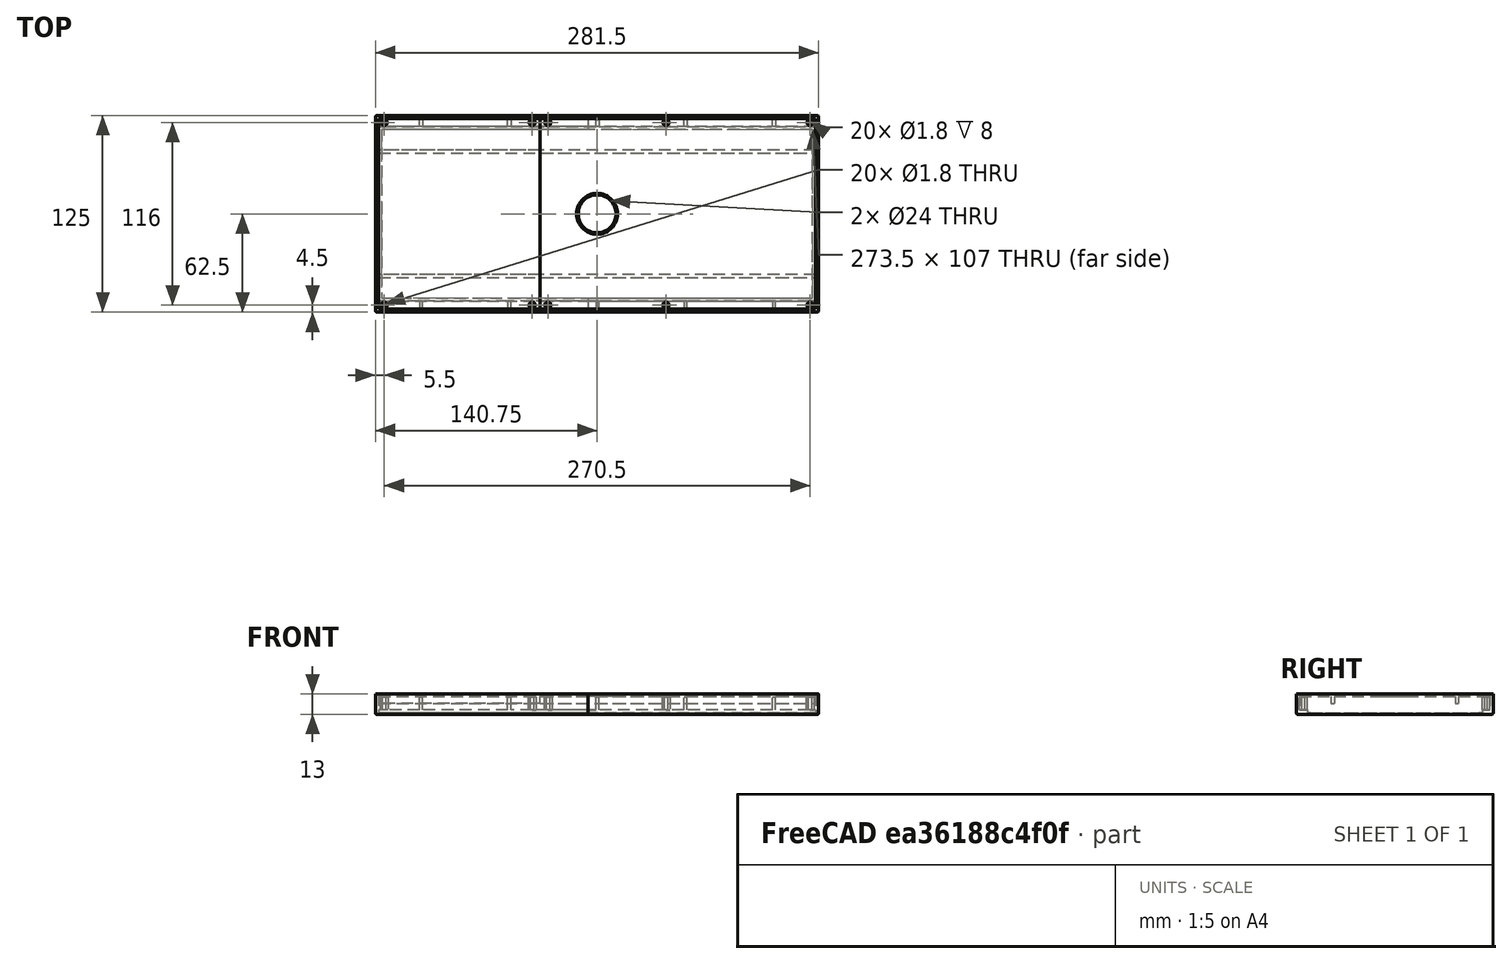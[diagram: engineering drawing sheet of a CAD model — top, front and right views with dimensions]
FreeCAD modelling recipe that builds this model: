
FCSTD DOCUMENT  (FreeCAD 0.20R29177 +426 (Git))
Label: Multisolarpanel-Screws
License: All rights reserved
LicenseURL: http://en.wikipedia.org/wiki/All_rights_reserved
objects: Sketcher::SketchObject×10, PartDesign::Pocket×6, Part::FeaturePython×6, PartDesign::Pad×4, Spreadsheet::Sheet×2, PartDesign::Plane×2, PartDesign::Body×2, App::DocumentObjectGroup×2, PartDesign::Chamfer×1, PartDesign::Fillet×1
note: 44 computed .brp shape members not serialized (recipe doc carries the construction recipe); baked Part::Feature solids carry a one-line shape summary decoded from their .brp

FEATURE [Spreadsheet::Sheet] Spreadsheet  label="Globals"
  cells = A2=Number of Panels; B2(NumberOfPanels)=5; A3=Panel Length; B3(PanelLength)==111mm; A4=Panel Width; B4(PanelWidth)==55mm; A5=Panel Height; B5(PanelHeight)==3.5mm; A7=Frame Width; B7(FrameWidth)==2mm; A8=Frame Height; B8(FrameHeight)==PlexiglasHeight + ScrewFixHeight + FrameWidth + 1mm; D8=Calculated; A9=Plexiglas Height; B9(PlexiglasHeight)==2mm; A10=Plexiglas Length; B10(PlexiglasLength)==(PanelWidth + FitPrecision) * NumberOfPanels; D10=Calculated; A11=Plexiglas Width; B11(PlexiglasWidth)==PanelLength; D11=Calculated; A12=Bottom Height (calculated); B12(BottomHeight)==FrameHeight - PlexiglasHeight - PanelHeight; D12=Calculated; A14=ScrewR; B14(ScrewR)==1mm; A15=ScrewFixHeight; B15(ScrewFixHeight)==8mm; A16=ScrewFixR; B16(ScrewFixR)==2.5mm; A18=BackPanel Width; B18(BackPanelWidth)==(PanelWidth + FitPrecision) * NumberOfPanels / 3; A22=Corner Length; B22(CornerLength)==5mm; A23=Corner Width; B23(CornerWidth)==1.5mm; A24=Corner Height; B24(CornerHeight)==PanelHeight; D24=Calculated; A25=Fit Precision; B25(FitPrecision)==0.5mm; A27=Connector Diameter; B27(ConnectorDiameter)==4.9mm; A29=FixThickness; B29(FixThickness)==2mm; A30=FixOuter (calculated); B30==PanelWidth + 2 * FrameWidth; D30=Calculated; A31=FixHeight; B31(FixHeight)==6mm; A32=HandsLength; B32(HandsLength)==4mm; A33=HandsDiameter; B33(HandsDiameter)==2mm; A35=BayonetInner; B35(BayonetInner)==B30 - 2 * FixThickness; D35=Calculated; A36=BayonetHeight; B36(BayonetHeight)==10mm
FEATURE [Spreadsheet::Sheet] Spreadsheet001  label="BayonetVars"
  cells = A2=InnerOuterRingR; B2(InnerOuterRingR)==20mm; A3=InnerRingWidth; B3(InnerRingWidth)==8mm; A4=InnerRingHeight; B4(InnerRingHeight)==15mm; A5=InnerBaseHeight; B5(InnerBaseHeight)==2mm; A6=OuterRingWidth; B6(OuterRingWidth)==5mm; A7=OuterRingHeight; B7(OuterRingHeight)==InnerRingHeight; A8=PinR; B8(PinR)==5mm; A9=PinDownPath; B9(PinDownPath)==InnerRingHeight / 2; A10=NumberOfPins; B10(NumberOfPins)=3; A11=FitPrecision; B11(FitPrecision)==0.5mm
FEATURE [Sketcher::SketchObject] Sketch012  label="WindowBase"
  FullyConstrained = true
  MapMode = 5
  Support = -> [XY_Plane003]
  expr: Constraints[10] = <<Globals>>.PlexiglasLength + <<Globals>>.FrameWidth * 2
  expr: Constraints[11] = <<Globals>>.PlexiglasWidth + <<Globals>>.ScrewFixR * 4 + <<Globals>>.FrameWidth * 2
  sketch-geometry (5):
    g0: LineSegment StartX=140.75 StartY=-62.5 StartZ=0 EndX=140.75 EndY=62.5 EndZ=0
    g1: LineSegment StartX=140.75 StartY=62.5 StartZ=0 EndX=-140.75 EndY=62.5 EndZ=0
    g2: LineSegment StartX=-140.75 StartY=62.5 StartZ=0 EndX=-140.75 EndY=-62.5 EndZ=0
    g3: LineSegment StartX=-140.75 StartY=-62.5 StartZ=0 EndX=140.75 EndY=-62.5 EndZ=0
    g4: GeomPoint X=0 Y=0 Z=0
  constraints (12):
    c: Coincident(g0,g1)
    c: Coincident(g1,g2)
    c: Coincident(g2,g3)
    c: Coincident(g3,g0)
    c: Horizontal(g1)
    c: Horizontal(g3)
    c: Vertical(g0)
    c: Vertical(g2)
    c: Symmetric(g1,g0,g4)
    c: Coincident(g4,g-1)
    c: DistanceX(g1,g1) = 281.5
    c: DistanceY(g2,g2) = 125
FEATURE [PartDesign::Pad] Pad006  label="TopBase"
  Direction = (0,0,1)
  Length = 13
  Length2 = 10
  Profile = -> Sketch012
  ReferenceAxis = -> Sketch012 [N_Axis]
  Refine = true
  Type = 0
  expr: Length = <<Globals>>.FrameHeight
FEATURE [Sketcher::SketchObject] Sketch013  label="PlexiglasSketch"
  FullyConstrained = true
  MapMode = 5
  Placement = pos=(0,0,13) rot=(0,0,1;0rad)
  Support = -> [Pad006]
  expr: Constraints[10] = <<Globals>>.PlexiglasLength
  expr: Constraints[11] = <<Globals>>.PlexiglasWidth
  sketch-geometry (5):
    g0: LineSegment StartX=138.75 StartY=-55.5 StartZ=0 EndX=138.75 EndY=55.5 EndZ=0
    g1: LineSegment StartX=138.75 StartY=55.5 StartZ=0 EndX=-138.75 EndY=55.5 EndZ=0
    g2: LineSegment StartX=-138.75 StartY=55.5 StartZ=0 EndX=-138.75 EndY=-55.5 EndZ=0
    g3: LineSegment StartX=-138.75 StartY=-55.5 StartZ=0 EndX=138.75 EndY=-55.5 EndZ=0
    g4: GeomPoint X=0 Y=0 Z=0
  constraints (12):
    c: Coincident(g0,g1)
    c: Coincident(g1,g2)
    c: Coincident(g2,g3)
    c: Coincident(g3,g0)
    c: Horizontal(g1)
    c: Horizontal(g3)
    c: Vertical(g0)
    c: Vertical(g2)
    c: Symmetric(g1,g0,g4)
    c: Coincident(g4,g-1)
    c: DistanceX(g1,g1) = 277.5
    c: DistanceY(g2,g2) = 111
FEATURE [PartDesign::Pocket] Pocket003  label="PlexiglasBase"
  BaseFeature = -> Pad006
  Direction = (0,0,-1)
  Length = 12
  Length2 = 5
  Profile = -> Sketch013
  ReferenceAxis = -> Sketch013 [N_Axis]
  Refine = true
  Type = 0
  expr: Length = <<Globals>>.FrameHeight - 1mm
FEATURE [Sketcher::SketchObject] Sketch014  label="WindowSketch"
  FullyConstrained = true
  MapMode = 5
  Placement = pos=(0,0,1) rot=(0,0,1;0rad)
  Support = -> [Pocket003]
  expr: Constraints[10] = <<Globals>>.PlexiglasLength - <<Globals>>.FrameWidth * 2
  expr: Constraints[11] = <<Globals>>.PlexiglasWidth - <<Globals>>.FrameWidth * 2
  sketch-geometry (5):
    g0: LineSegment StartX=136.75 StartY=-53.5 StartZ=0 EndX=136.75 EndY=53.5 EndZ=0
    g1: LineSegment StartX=136.75 StartY=53.5 StartZ=0 EndX=-136.75 EndY=53.5 EndZ=0
    g2: LineSegment StartX=-136.75 StartY=53.5 StartZ=0 EndX=-136.75 EndY=-53.5 EndZ=0
    g3: LineSegment StartX=-136.75 StartY=-53.5 StartZ=0 EndX=136.75 EndY=-53.5 EndZ=0
    g4: GeomPoint X=0 Y=0 Z=0
  constraints (12):
    c: Coincident(g0,g1)
    c: Coincident(g1,g2)
    c: Coincident(g2,g3)
    c: Coincident(g3,g0)
    c: Horizontal(g1)
    c: Horizontal(g3)
    c: Vertical(g0)
    c: Vertical(g2)
    c: Symmetric(g1,g0,g4)
    c: Coincident(g4,g-1)
    c: DistanceX(g1,g1) = 273.5
    c: DistanceY(g2,g2) = 107
FEATURE [PartDesign::Pocket] Pocket004  label="Window"
  BaseFeature = -> Pocket003
  Direction = (0,0,-1)
  Length = 5
  Length2 = 5
  Profile = -> Sketch014
  ReferenceAxis = -> Sketch014 [N_Axis]
  Refine = true
  Type = 1
FEATURE [Sketcher::SketchObject] Sketch015  label="FrameSketch"
  FullyConstrained = true
  MapMode = 5
  Placement = pos=(0,0,13) rot=(0,0,1;0rad)
  Support = -> [Pocket004]
  expr: .Constraints.FrameLength = <<Globals>>.PlexiglasLength
  expr: .Constraints.FrameWidth = <<Globals>>.PlexiglasWidth + <<Globals>>.ScrewFixR * 4
  sketch-geometry (5):
    g0: LineSegment StartX=138.75 StartY=-60.5 StartZ=0 EndX=138.75 EndY=60.5 EndZ=0
    g1: LineSegment StartX=138.75 StartY=60.5 StartZ=0 EndX=-138.75 EndY=60.5 EndZ=0
    g2: LineSegment StartX=-138.75 StartY=60.5 StartZ=0 EndX=-138.75 EndY=-60.5 EndZ=0
    g3: LineSegment StartX=-138.75 StartY=-60.5 StartZ=0 EndX=138.75 EndY=-60.5 EndZ=0
    g4: GeomPoint X=0 Y=0 Z=0
  constraints (12):
    c: Coincident(g0,g1)
    c: Coincident(g1,g2)
    c: Coincident(g2,g3)
    c: Coincident(g3,g0)
    c: Horizontal(g1)
    c: Horizontal(g3)
    c: Vertical(g0)
    c: Vertical(g2)
    c: Symmetric(g1,g0,g4)
    c: Coincident(g4,g-1)
    c: DistanceX(g1,g1) = 277.5  'FrameLength'
    c: DistanceY(g2,g2) = 121  'FrameWidth'
FEATURE [PartDesign::Pocket] Pocket005  label="Frame"
  BaseFeature = -> Pocket004
  Direction = (0,0,-1)
  Length = 10
  Length2 = 5
  Profile = -> Sketch015
  ReferenceAxis = -> Sketch015 [N_Axis]
  Refine = true
  Type = 0
  expr: Length = <<Globals>>.FrameHeight - <<Globals>>.PlexiglasHeight - 1mm
FEATURE [Sketcher::SketchObject] Sketch016  label="ScrewFixesAndPanelGuidesSketch"
  ExternalGeometry = -> [Sketch015]
  FullyConstrained = false
  MapMode = 5
  Placement = pos=(0,0,3) rot=(0,0,1;0rad)
  Support = -> [Pocket005]
  expr: Constraints[0] = <<Globals>>.ScrewFixR
  expr: Constraints[29] = <<Globals>>.ScrewFixR + 1mm
  expr: Constraints[39] = <<Globals>>.ScrewFixR * 2
  expr: Constraints[40] = <<Globals>>.FrameWidth
  sketch-geometry (51):
    g0: Circle CenterX=-135.25 CenterY=58 CenterZ=0 NormalX=0 NormalY=0 NormalZ=1 AngleXU=0 Radius=2.5
    g1: Circle CenterX=-135.25 CenterY=-58 CenterZ=0 NormalX=0 NormalY=0 NormalZ=1 AngleXU=0 Radius=2.5
    g2: Circle CenterX=-41.25 CenterY=58 CenterZ=0 NormalX=0 NormalY=0 NormalZ=1 AngleXU=0 Radius=2.5
    g3: Circle CenterX=43.75 CenterY=58 CenterZ=0 NormalX=0 NormalY=0 NormalZ=1 AngleXU=0 Radius=2.5
    g4: Circle CenterX=-41.25 CenterY=-58 CenterZ=0 NormalX=0 NormalY=0 NormalZ=1 AngleXU=0 Radius=2.5
    g5: Circle CenterX=43.75 CenterY=-58 CenterZ=0 NormalX=0 NormalY=0 NormalZ=1 AngleXU=0 Radius=2.5
    g6: Circle CenterX=135.25 CenterY=58 CenterZ=0 NormalX=0 NormalY=0 NormalZ=1 AngleXU=0 Radius=2.5
    g7: Circle CenterX=135.25 CenterY=-58 CenterZ=0 NormalX=0 NormalY=0 NormalZ=1 AngleXU=0 Radius=2.5
    g8: GeomPoint X=-137.75 Y=58 Z=0
    g9: Circle CenterX=-31.25 CenterY=58 CenterZ=0 NormalX=0 NormalY=0 NormalZ=1 AngleXU=0 Radius=2.5
    g10: Circle CenterX=-31.25 CenterY=-58 CenterZ=0 NormalX=0 NormalY=0 NormalZ=1 AngleXU=0 Radius=2.5
    g11: LineSegment StartX=-112.75 StartY=60.5 StartZ=0 EndX=-110.75 EndY=60.5 EndZ=0
    g12: LineSegment StartX=-110.75 StartY=60.5 StartZ=0 EndX=-110.75 EndY=55.5 EndZ=0
    g13: LineSegment StartX=-110.75 StartY=55.5 StartZ=0 EndX=-112.75 EndY=55.5 EndZ=0
    g14: LineSegment StartX=-112.75 StartY=55.5 StartZ=0 EndX=-112.75 EndY=60.5 EndZ=0
    g15: LineSegment StartX=-56.75 StartY=60.5 StartZ=0 EndX=-54.75 EndY=60.5 EndZ=0
    g16: LineSegment StartX=-54.75 StartY=60.5 StartZ=0 EndX=-54.75 EndY=55.5 EndZ=0
    g17: LineSegment StartX=-54.75 StartY=55.5 StartZ=0 EndX=-56.75 EndY=55.5 EndZ=0
    g18: LineSegment StartX=-56.75 StartY=55.5 StartZ=0 EndX=-56.75 EndY=60.5 EndZ=0
    g19: LineSegment StartX=-0.75 StartY=60.5 StartZ=0 EndX=1.25 EndY=60.5 EndZ=0
    g20: LineSegment StartX=1.25 StartY=60.5 StartZ=0 EndX=1.25 EndY=55.5 EndZ=0
    g21: LineSegment StartX=1.25 StartY=55.5 StartZ=0 EndX=-0.75 EndY=55.5 EndZ=0
    g22: LineSegment StartX=-0.75 StartY=55.5 StartZ=0 EndX=-0.75 EndY=60.5 EndZ=0
    g23: LineSegment StartX=55.25 StartY=60.5 StartZ=0 EndX=57.25 EndY=60.5 EndZ=0
    g24: LineSegment StartX=57.25 StartY=60.5 StartZ=0 EndX=57.25 EndY=55.5 EndZ=0
    g25: LineSegment StartX=57.25 StartY=55.5 StartZ=0 EndX=55.25 EndY=55.5 EndZ=0
    g26: LineSegment StartX=55.25 StartY=55.5 StartZ=0 EndX=55.25 EndY=60.5 EndZ=0
    g27: LineSegment StartX=111.25 StartY=60.5 StartZ=0 EndX=113.25 EndY=60.5 EndZ=0
    g28: LineSegment StartX=113.25 StartY=60.5 StartZ=0 EndX=113.25 EndY=55.5 EndZ=0
    g29: LineSegment StartX=113.25 StartY=55.5 StartZ=0 EndX=111.25 EndY=55.5 EndZ=0
    g30: LineSegment StartX=111.25 StartY=55.5 StartZ=0 EndX=111.25 EndY=60.5 EndZ=0
    g31: LineSegment StartX=-112.75 StartY=-60.5 StartZ=0 EndX=-110.75 EndY=-60.5 EndZ=0
    g32: LineSegment StartX=-110.75 StartY=-60.5 StartZ=0 EndX=-110.75 EndY=-55.5 EndZ=0
    g33: LineSegment StartX=-110.75 StartY=-55.5 StartZ=0 EndX=-112.75 EndY=-55.5 EndZ=0
    g34: LineSegment StartX=-112.75 StartY=-55.5 StartZ=0 EndX=-112.75 EndY=-60.5 EndZ=0
    g35: LineSegment StartX=-56.75 StartY=-60.5 StartZ=0 EndX=-54.75 EndY=-60.5 EndZ=0
    g36: LineSegment StartX=-54.75 StartY=-60.5 StartZ=0 EndX=-54.75 EndY=-55.5 EndZ=0
    g37: LineSegment StartX=-54.75 StartY=-55.5 StartZ=0 EndX=-56.75 EndY=-55.5 EndZ=0
    g38: LineSegment StartX=-56.75 StartY=-55.5 StartZ=0 EndX=-56.75 EndY=-60.5 EndZ=0
    g39: LineSegment StartX=-0.75 StartY=-60.5 StartZ=0 EndX=1.25 EndY=-60.5 EndZ=0
    g40: LineSegment StartX=1.25 StartY=-60.5 StartZ=0 EndX=1.25 EndY=-55.5 EndZ=0
    g41: LineSegment StartX=1.25 StartY=-55.5 StartZ=0 EndX=-0.75 EndY=-55.5 EndZ=0
    g42: LineSegment StartX=-0.75 StartY=-55.5 StartZ=0 EndX=-0.75 EndY=-60.5 EndZ=0
    g43: LineSegment StartX=55.25 StartY=-60.5 StartZ=0 EndX=57.25 EndY=-60.5 EndZ=0
    g44: LineSegment StartX=57.25 StartY=-60.5 StartZ=0 EndX=57.25 EndY=-55.5 EndZ=0
    g45: LineSegment StartX=57.25 StartY=-55.5 StartZ=0 EndX=55.25 EndY=-55.5 EndZ=0
    g46: LineSegment StartX=55.25 StartY=-55.5 StartZ=0 EndX=55.25 EndY=-60.5 EndZ=0
    g47: LineSegment StartX=111.25 StartY=-60.5 StartZ=0 EndX=113.25 EndY=-60.5 EndZ=0
    g48: LineSegment StartX=113.25 StartY=-60.5 StartZ=0 EndX=113.25 EndY=-55.5 EndZ=0
    g49: LineSegment StartX=113.25 StartY=-55.5 StartZ=0 EndX=111.25 EndY=-55.5 EndZ=0
    g50: LineSegment StartX=111.25 StartY=-55.5 StartZ=0 EndX=111.25 EndY=-60.5 EndZ=0
  constraints (132):
    c: Radius(g0) = 2.5
    c: Radius(g1) = 2.5
    c: Equal(g0,g2) = 2.5
    c: PointOnObject(g8,g0)
    c: DistanceX(g-3,g8) = 1  'X_Off_1'
    c: Vertical(g2,g4)
    c: Vertical(g0,g1)
    c: Vertical(g3,g5)
    c: Vertical(g6,g7)
    c: Horizontal(g6,g3)
    c: Horizontal(g3,g2)
    c: Horizontal(g2,g0)
    c: Equal(g2,g3)
    c: Equal(g3,g6)
    c: Equal(g6,g7)
    c: Equal(g7,g5)
    c: Equal(g5,g4)
    c: DistanceX(g0,g2) = 94  'X_Off_2'
    c: Horizontal(g1,g4)
    c: Horizontal(g4,g5)
    c: Horizontal(g5,g7)
    c: Tangent(g-4,g1)
    c: Equal(g2,g9)
    c: Horizontal(g9,g2)
    c: DistanceX(g2,g9) = 10  'X_Off_3'
    c: Equal(g10,g4)
    c: Horizontal(g10,g4)
    c: Vertical(g10,g9)
    c: Tangent(g0,g-6)
    c: DistanceX(g6,g-6) = 3.5
    c: Coincident(g11,g12)
    c: Coincident(g12,g13)
    c: Coincident(g13,g14)
    c: Coincident(g14,g11)
    c: Horizontal(g11)
    c: Horizontal(g13)
    c: Vertical(g12)
    c: Vertical(g14)
    c: PointOnObject(g11,g-6)
    c: DistanceY(g14,g14) = 5
    c: DistanceX(g13,g13) = 2
    c: DistanceX(g-6,g11) = 26
    c: Coincident(g15,g16)
    c: Coincident(g16,g17)
    c: Coincident(g17,g18)
    c: Coincident(g18,g15)
    c: Horizontal(g17)
    c: Vertical(g16)
    c: Vertical(g18)
    c: Equal(g14,g18) = 5
    c: Equal(g13,g17) = 2
    c: Coincident(g19,g20)
    c: Coincident(g20,g21)
    c: Coincident(g21,g22)
    c: Coincident(g22,g19)
    c: Horizontal(g21)
    c: Vertical(g20)
    c: Vertical(g22)
    c: Equal(g14,g22) = 5
    c: Equal(g13,g21) = 2
    c: Coincident(g23,g24)
    c: Coincident(g24,g25)
    c: Coincident(g25,g26)
    c: Coincident(g26,g23)
    c: Horizontal(g25)
    c: Vertical(g24)
    c: Vertical(g26)
    c: Equal(g14,g26) = 5
    c: Equal(g13,g25) = 2
    c: Coincident(g27,g28)
    c: Coincident(g28,g29)
    c: Coincident(g29,g30)
    c: Coincident(g30,g27)
    c: Horizontal(g29)
    c: Vertical(g28)
    c: Vertical(g30)
    c: Equal(g14,g30) = 5
    c: Equal(g13,g29) = 2
    c: Tangent(g27,g-6)
    c: Tangent(g23,g-6)
    c: Tangent(g19,g-6)
    c: Tangent(g-6,g15)
    c: DistanceX(g11,g15) = 56
    c: DistanceX(g15,g19) = 56
    c: DistanceX(g19,g23) = 56
    c: DistanceX(g23,g27) = 56
    c: Coincident(g31,g32)
    c: Coincident(g32,g33)
    c: Coincident(g33,g34)
    c: Coincident(g34,g31)
    c: Horizontal(g31)
    c: Horizontal(g33)
    c: Vertical(g32)
    c: Vertical(g34)
    c: Coincident(g35,g36)
    c: Coincident(g36,g37)
    c: Coincident(g37,g38)
    c: Coincident(g38,g35)
    c: Horizontal(g37)
    c: Vertical(g36)
    c: Vertical(g38)
    c: Equal(g34,g38) = 5
    c: Equal(g33,g37) = 2
    c: Coincident(g39,g40)
    c: Coincident(g40,g41)
    c: Coincident(g41,g42)
    c: Coincident(g42,g39)
    c: Horizontal(g41)
    c: Vertical(g40)
    c: Vertical(g42)
    c: Equal(g34,g42) = 5
    c: Equal(g33,g41) = 2
    c: Coincident(g43,g44)
    c: Coincident(g44,g45)
    c: Coincident(g45,g46)
    c: Coincident(g46,g43)
    c: Horizontal(g45)
    c: Vertical(g44)
    c: Vertical(g46)
    c: Equal(g34,g46) = 5
    c: Equal(g33,g45) = 2
    c: Coincident(g47,g48)
    c: Coincident(g48,g49)
    c: Coincident(g49,g50)
    c: Coincident(g50,g47)
    c: Horizontal(g49)
    c: Vertical(g48)
    c: Vertical(g50)
    c: Equal(g34,g50) = 5
    c: Equal(g33,g49) = 2
    c: Horizontal(g0,g8)
    c: DistanceX(g9,g3) = 75  'X_Off_4'
FEATURE [PartDesign::Pad] Pad  label="ScrewFixesAndPanelGuides"
  BaseFeature = -> Pocket005
  Direction = (0,0,1)
  Length = 8
  Length2 = 10
  Profile = -> Sketch016
  ReferenceAxis = -> Sketch016 [N_Axis]
  Refine = true
  Type = 0
  expr: Length = <<Globals>>.ScrewFixHeight
FEATURE [Sketcher::SketchObject] Sketch  label="ScrewHolesSketch"
  ExternalGeometry = -> [Sketch016]
  FullyConstrained = true
  MapMode = 5
  Placement = pos=(0,0,11) rot=(0,0,1;0rad)
  Support = -> [Pad]
  expr: Constraints[19] = <<Globals>>.ScrewR - 0.1mm
  sketch-geometry (10):
    g0: Circle CenterX=-135.25 CenterY=58 CenterZ=0 NormalX=0 NormalY=0 NormalZ=1 AngleXU=0 Radius=0.9
    g1: Circle CenterX=-41.25 CenterY=58 CenterZ=0 NormalX=0 NormalY=0 NormalZ=1 AngleXU=0 Radius=0.9
    g2: Circle CenterX=-31.25 CenterY=58 CenterZ=0 NormalX=0 NormalY=0 NormalZ=1 AngleXU=0 Radius=0.9
    g3: Circle CenterX=43.75 CenterY=58 CenterZ=0 NormalX=0 NormalY=0 NormalZ=1 AngleXU=0 Radius=0.9
    g4: Circle CenterX=135.25 CenterY=58 CenterZ=0 NormalX=0 NormalY=0 NormalZ=1 AngleXU=0 Radius=0.9
    g5: Circle CenterX=135.25 CenterY=-58 CenterZ=0 NormalX=0 NormalY=0 NormalZ=1 AngleXU=0 Radius=0.9
    g6: Circle CenterX=43.75 CenterY=-58 CenterZ=0 NormalX=0 NormalY=0 NormalZ=1 AngleXU=0 Radius=0.9
    g7: Circle CenterX=-31.25 CenterY=-58 CenterZ=0 NormalX=0 NormalY=0 NormalZ=1 AngleXU=0 Radius=0.9
    g8: Circle CenterX=-41.25 CenterY=-58 CenterZ=0 NormalX=0 NormalY=0 NormalZ=1 AngleXU=0 Radius=0.9
    g9: Circle CenterX=-135.25 CenterY=-58 CenterZ=0 NormalX=0 NormalY=0 NormalZ=1 AngleXU=0 Radius=0.9
  constraints (20):
    c: Coincident(g0,g-3)
    c: Coincident(g1,g-4)
    c: Coincident(g2,g-11)
    c: Coincident(g3,g-5)
    c: Coincident(g4,g-6)
    c: Coincident(g5,g-7)
    c: Coincident(g6,g-8)
    c: Coincident(g7,g-12)
    c: Coincident(g8,g-9)
    c: Coincident(g9,g-10)
    c: Equal(g0,g1)
    c: Equal(g1,g2)
    c: Equal(g2,g3)
    c: Equal(g3,g4)
    c: Equal(g4,g5)
    c: Equal(g5,g6)
    c: Equal(g6,g7)
    c: Equal(g7,g8)
    c: Equal(g8,g9)
    c: Radius(g0) = 0.9
FEATURE [PartDesign::Pocket] Pocket  label="ScrewHoles"
  BaseFeature = -> Pad
  Direction = (0,0,-1)
  Length = 8
  Length2 = 5
  Profile = -> Sketch
  ReferenceAxis = -> Sketch [N_Axis]
  Refine = true
  Type = 0
  expr: Length = <<Globals>>.ScrewFixHeight
FEATURE [Sketcher::SketchObject] Sketch017  label="BackPlaneSketch"
  FullyConstrained = true
  MapMode = 5
  Placement = pos=(0,0,13) rot=(0,0,1;0rad)
  expr: Constraints[10] = <<FrameSketch>>.Constraints.FrameLength
  expr: Constraints[11] = <<FrameSketch>>.Constraints.FrameWidth
  sketch-geometry (5):
    g0: LineSegment StartX=138.75 StartY=-60.5 StartZ=0 EndX=138.75 EndY=60.5 EndZ=0
    g1: LineSegment StartX=138.75 StartY=60.5 StartZ=0 EndX=-138.75 EndY=60.5 EndZ=0
    g2: LineSegment StartX=-138.75 StartY=60.5 StartZ=0 EndX=-138.75 EndY=-60.5 EndZ=0
    g3: LineSegment StartX=-138.75 StartY=-60.5 StartZ=0 EndX=138.75 EndY=-60.5 EndZ=0
    g4: GeomPoint X=0 Y=0 Z=0
  constraints (12):
    c: Coincident(g0,g1)
    c: Coincident(g1,g2)
    c: Coincident(g2,g3)
    c: Coincident(g3,g0)
    c: Horizontal(g1)
    c: Horizontal(g3)
    c: Vertical(g0)
    c: Vertical(g2)
    c: Symmetric(g1,g0,g4)
    c: Coincident(g4,g-1)
    c: DistanceX(g1,g1) = 277.5
    c: DistanceY(g2,g2) = 121
FEATURE [PartDesign::Pad] Pad007  label="BackPlane"
  Direction = (0,0,1)
  Length = 1.5
  Length2 = 10
  Placement = pos=(0,0,13) rot=(0,0,1;0rad)
  Profile = -> Sketch017
  ReferenceAxis = -> Sketch017 [N_Axis]
  Refine = true
  Reversed = true
  Type = 0
FEATURE [Sketcher::SketchObject] Sketch018  label="ScrewHolesSketch001"
  ExternalGeometry = -> [Sketch017]
  FullyConstrained = true
  MapMode = 5
  Placement = pos=(0,0,11.5) rot=(1,0,0;3.14159rad)
  Support = -> [Pad007]
  expr: Constraints[10] = <<ScrewFixesAndPanelGuidesSketch>>.Constraints.X_Off_1 + <<Globals>>.ScrewFixR
  expr: Constraints[11] = <<ScrewFixesAndPanelGuidesSketch>>.Constraints.X_Off_2
  expr: Constraints[12] = <<ScrewFixesAndPanelGuidesSketch>>.Constraints.X_Off_3
  expr: Constraints[13] = <<ScrewFixesAndPanelGuidesSketch>>.Constraints.X_Off_4
  expr: Constraints[14] = <<ScrewFixesAndPanelGuidesSketch>>.Constraints.X_Off_1 + <<Globals>>.ScrewFixR
  expr: Constraints[19] = <<Globals>>.ScrewFixR
  expr: Constraints[28] = <<Globals>>.ScrewFixR
  expr: Constraints[9] = <<Globals>>.ScrewR - 0.1mm
  sketch-geometry (10):
    g0: Circle CenterX=-135.25 CenterY=58 CenterZ=0 NormalX=0 NormalY=0 NormalZ=1 AngleXU=0 Radius=0.9
    g1: Circle CenterX=-41.25 CenterY=58 CenterZ=0 NormalX=0 NormalY=0 NormalZ=1 AngleXU=0 Radius=0.9
    g2: Circle CenterX=-31.25 CenterY=58 CenterZ=0 NormalX=0 NormalY=0 NormalZ=1 AngleXU=0 Radius=0.9
    g3: Circle CenterX=43.75 CenterY=58 CenterZ=0 NormalX=0 NormalY=0 NormalZ=1 AngleXU=0 Radius=0.9
    g4: Circle CenterX=135.25 CenterY=58 CenterZ=0 NormalX=0 NormalY=0 NormalZ=1 AngleXU=0 Radius=0.9
    g5: Circle CenterX=135.25 CenterY=-58 CenterZ=0 NormalX=0 NormalY=0 NormalZ=1 AngleXU=0 Radius=0.9
    g6: Circle CenterX=43.75 CenterY=-58 CenterZ=0 NormalX=0 NormalY=0 NormalZ=1 AngleXU=0 Radius=0.9
    g7: Circle CenterX=-31.25 CenterY=-58 CenterZ=0 NormalX=0 NormalY=0 NormalZ=1 AngleXU=0 Radius=0.9
    g8: Circle CenterX=-41.25 CenterY=-58 CenterZ=0 NormalX=0 NormalY=0 NormalZ=1 AngleXU=0 Radius=0.9
    g9: Circle CenterX=-135.25 CenterY=-58 CenterZ=0 NormalX=0 NormalY=0 NormalZ=1 AngleXU=0 Radius=0.9
  constraints (30):
    c: Equal(g0,g1)
    c: Equal(g1,g2)
    c: Equal(g2,g3)
    c: Equal(g3,g4)
    c: Equal(g4,g5)
    c: Equal(g5,g6)
    c: Equal(g6,g7)
    c: Equal(g7,g8)
    c: Equal(g8,g9)
    c: Radius(g0) = 0.9
    c: DistanceX(g-4,g0) = 3.5
    c: DistanceX(g0,g1) = 94
    c: DistanceX(g1,g2) = 10
    c: DistanceX(g2,g3) = 75
    c: DistanceX(g4,g-5) = 3.5
    c: Horizontal(g4,g3)
    c: Horizontal(g3,g2)
    c: Horizontal(g2,g1)
    c: Horizontal(g1,g0)
    c: DistanceY(g0,g-4) = 2.5
    c: Vertical(g0,g9)
    c: Vertical(g1,g8)
    c: Vertical(g7,g2)
    c: Vertical(g3,g6)
    c: Vertical(g4,g5)
    c: Horizontal(g5,g6)
    c: Horizontal(g6,g8)
    c: Horizontal(g8,g9)
    c: DistanceY(g-6,g9) = 2.5
    c: Horizontal(g7,g8)
FEATURE [PartDesign::Pocket] Pocket006  label="PlaneWithScrewHoles"
  BaseFeature = -> Pad007
  Direction = (0,0,1)
  Length = 5
  Length2 = 5
  Placement = pos=(0,0,13) rot=(0,0,1;0rad)
  Profile = -> Sketch018
  ReferenceAxis = -> Sketch018 [N_Axis]
  Refine = true
  Type = 1
FEATURE [Sketcher::SketchObject] Sketch025
  ExternalGeometry = -> [Pocket006]
  FullyConstrained = true
  MapMode = 5
  Placement = pos=(0,0,11.5) rot=(1,0,0;3.14159rad)
  Support = -> [Pocket006]
  expr: Constraints[21] = <<Globals>>.FrameWidth
  expr: Constraints[22] = <<Globals>>.FrameWidth
  sketch-geometry (8):
    g0: LineSegment StartX=-138.75 StartY=40.5 StartZ=0 EndX=138.75 EndY=40.5 EndZ=0
    g1: LineSegment StartX=138.75 StartY=40.5 StartZ=0 EndX=138.75 EndY=38.5 EndZ=0
    g2: LineSegment StartX=138.75 StartY=38.5 StartZ=0 EndX=-138.75 EndY=38.5 EndZ=0
    g3: LineSegment StartX=-138.75 StartY=38.5 StartZ=0 EndX=-138.75 EndY=40.5 EndZ=0
    g4: LineSegment StartX=-138.75 StartY=-38.5 StartZ=0 EndX=138.75 EndY=-38.5 EndZ=0
    g5: LineSegment StartX=138.75 StartY=-38.5 StartZ=0 EndX=138.75 EndY=-40.5 EndZ=0
    g6: LineSegment StartX=138.75 StartY=-40.5 StartZ=0 EndX=-138.75 EndY=-40.5 EndZ=0
    g7: LineSegment StartX=-138.75 StartY=-40.5 StartZ=0 EndX=-138.75 EndY=-38.5 EndZ=0
  constraints (24):
    c: Coincident(g0,g1)
    c: Coincident(g1,g2)
    c: Coincident(g2,g3)
    c: Coincident(g3,g0)
    c: Horizontal(g0)
    c: Horizontal(g2)
    c: Vertical(g1)
    c: Vertical(g3)
    c: PointOnObject(g0,g-4)
    c: PointOnObject(g1,g-6)
    c: Coincident(g4,g5)
    c: Coincident(g5,g6)
    c: Coincident(g6,g7)
    c: Coincident(g7,g4)
    c: Horizontal(g4)
    c: Horizontal(g6)
    c: Vertical(g5)
    c: Vertical(g7)
    c: PointOnObject(g4,g-4)
    c: PointOnObject(g5,g-6)
    c: DistanceY(g-5,g6) = 20
    c: DistanceY(g6,g4) = 2
    c: DistanceY(g2,g0) = 2
    c: DistanceY(g0,g-4) = 20
FEATURE [PartDesign::Pad] Pad009  label="Rails"
  BaseFeature = -> Pocket006
  Direction = (0,0,-1)
  Length = 4.5
  Length2 = 10
  Placement = pos=(0,0,13) rot=(0,0,1;0rad)
  Profile = -> Sketch025
  ReferenceAxis = -> Sketch025 [N_Axis]
  Refine = true
  Type = 0
  expr: Length = <<Globals>>.ScrewFixHeight - <<Globals>>.PanelHeight
FEATURE [PartDesign::Plane] DatumPlane001  label="CutPlane2"
  AttachmentOffset = pos=(0,0,-102.5) rot=(0,0,1;0rad)
  Length = 136.556
  MapMode = 4
  Placement = pos=(-36.25,0,0) rot=(0.57735,-0.57735,-0.57735;2.0944rad)
  ResizeMode = 0
  Width = 65.5563
FEATURE [Sketcher::SketchObject] Sketch026  label="CableHoleSketch"
  FullyConstrained = true
  MapMode = 5
  Placement = pos=(0,0,13) rot=(0,0,1;0rad)
  Support = -> [Pad009]
  expr: Constraints[1] = <<BayonetVars>>.InnerOuterRingR - <<BayonetVars>>.InnerRingWidth
  sketch-geometry (1):
    g0: Circle CenterX=0 CenterY=0 CenterZ=0 NormalX=0 NormalY=0 NormalZ=1 AngleXU=0 Radius=12
  constraints (2):
    c: Coincident(g0,g-1)
    c: Radius(g0) = 12
FEATURE [PartDesign::Plane] DatumPlane  label="CutPlane1"
  AttachmentOffset = pos=(0,0,-135) rot=(0,0,1;0rad)
  Length = 140.811
  MapMode = 4
  Placement = pos=(-5.75,0,0) rot=(0.57735,-0.57735,-0.57735;2.0944rad)
  ResizeMode = 0
  Width = 65.8114
FEATURE [PartDesign::Pocket] Pocket007  label="CableHole"
  BaseFeature = -> Pad009
  Direction = (0,0,-1)
  Length = 5
  Length2 = 5
  Placement = pos=(0,0,13) rot=(0,0,1;0rad)
  Profile = -> Sketch026
  ReferenceAxis = -> Sketch026 [N_Axis]
  Refine = true
  Type = 1
FEATURE [PartDesign::Chamfer] Chamfer
  Angle = 45
  Base = -> Pocket007 [Edge32,Edge31,Edge30,Edge29,Edge28,Edge33,Edge34,Edge35,Edge37,Edge38,Edge36]
  BaseFeature = -> Pocket007
  ChamferType = 0
  FlipDirection = false
  Placement = pos=(0,0,13) rot=(0,0,1;0rad)
  Refine = true
  Size = 1
  Size2 = 1
  SupportTransform = false
  UseAllEdges = false
FEATURE [PartDesign::Body] Body  label="BackPanel"
  Group = -> [Sketch017,Pad007,Sketch018,Pocket006,Sketch025,Pad009,DatumPlane001,Sketch026,Pocket007,Chamfer]
  Origin = -> Origin
  Tip = -> Chamfer
FEATURE [PartDesign::Fillet] Fillet
  Base = -> Pocket [Edge217,Edge215,Edge216,Edge213,Edge214,Edge210,Edge212,Edge211]
  BaseFeature = -> Pocket
  Radius = 1
  Refine = true
  SupportTransform = false
  UseAllEdges = false
FEATURE [PartDesign::Body] Body003  label="ClosedPanelTop"
  Group = -> [Sketch012,Pad006,Sketch013,Pocket003,Sketch014,Pocket004,Sketch015,Pocket005,Sketch016,Pad,Sketch,Pocket,DatumPlane,Fillet]
  Origin = -> Origin003
  Tip = -> Fillet
FEATURE [Part::FeaturePython] Slice  # WARN: FeaturePython — macro-defined, semantics opaque (R4)
  Base = -> Chamfer
  Mode = 1
  Tolerance = 0
  Tools = -> [DatumPlane001]
FEATURE [Part::FeaturePython] Slice_child0  label="Slice.0"  # WARN: FeaturePython — macro-defined, semantics opaque (R4)
  Base = -> Slice
  FilterType = 1
  Invert = false
  OverrideMaxVal = 0
  WindowFrom = 80
  WindowTo = 100
  items = 0
FEATURE [Part::FeaturePython] Slice_child1  label="Slice.1"  # WARN: FeaturePython — macro-defined, semantics opaque (R4)
  Base = -> Slice
  FilterType = 1
  Invert = false
  OverrideMaxVal = 0
  WindowFrom = 80
  WindowTo = 100
  items = 1
FEATURE [App::DocumentObjectGroup] GrExplode_Slice  label="BackSlice"
  Group = -> [Slice_child0,Slice_child1]
FEATURE [Part::FeaturePython] Slice001  # WARN: FeaturePython — macro-defined, semantics opaque (R4)
  Base = -> Fillet
  Mode = 1
  Tolerance = 0
  Tools = -> [DatumPlane]
FEATURE [Part::FeaturePython] Slice001_child0  label="Slice001.0"  # WARN: FeaturePython — macro-defined, semantics opaque (R4)
  Base = -> Slice001
  FilterType = 1
  Invert = false
  OverrideMaxVal = 0
  WindowFrom = 80
  WindowTo = 100
  items = 0
FEATURE [Part::FeaturePython] Slice001_child1  label="Slice001.1"  # WARN: FeaturePython — macro-defined, semantics opaque (R4)
  Base = -> Slice001
  FilterType = 1
  Invert = false
  OverrideMaxVal = 0
  WindowFrom = 80
  WindowTo = 100
  items = 1
FEATURE [App::DocumentObjectGroup] GrExplode_Slice001  label="TopSlice"
  Group = -> [Slice001_child0,Slice001_child1]
